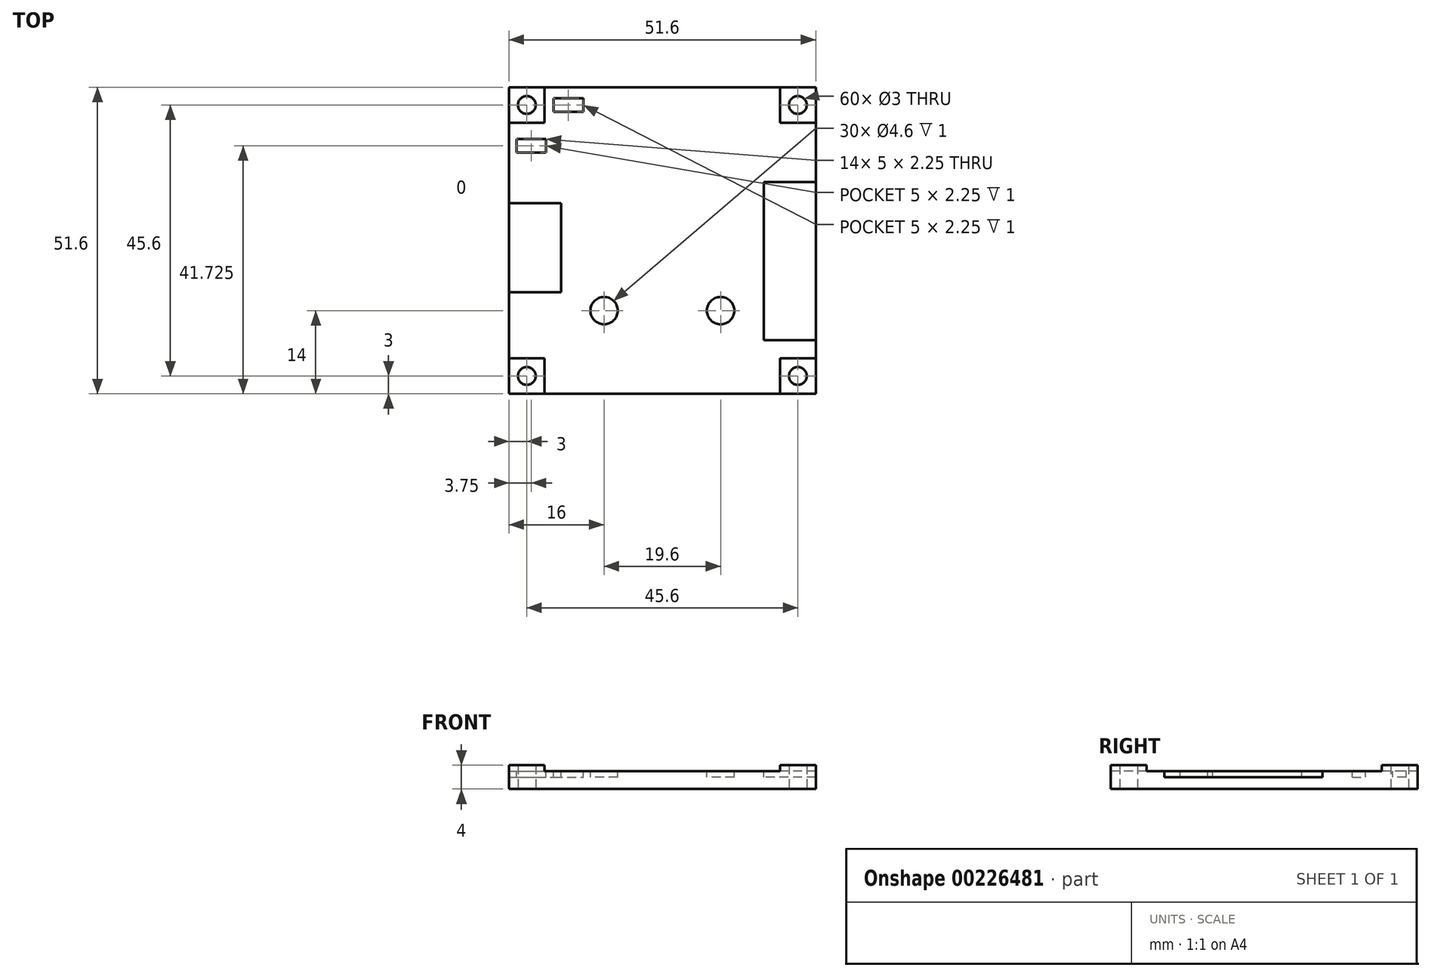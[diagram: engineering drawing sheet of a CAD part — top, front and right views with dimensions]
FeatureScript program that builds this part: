
annotation { "Feature Type Name" : "Feature", "Feature Type Description" : "" }
export const myFeature = defineFeature(function(context is Context, id is Id, definition is map)
    precondition{}
    {
        {
            var Q0;
            Q0=qCreatedBy(makeId("Top.planeOp"),FACE);
            var sketch = newSketch(context, id + "F0", { "sketchPlane" : qUnion([Q0])});
            skLineSegment(sketch, "E0.bottom", {"start": v(0, 0) * mm, "end": v(51.6, 0) * mm});
            skLineSegment(sketch, "E0.top", {"start": v(0, -51.6) * mm, "end": v(51.6, -51.6) * mm});
            skLineSegment(sketch, "E0.left", {"start": v(0, 0) * mm, "end": v(0, -51.6) * mm});
            skLineSegment(sketch, "E0.right", {"start": v(51.6, 0) * mm, "end": v(51.6, -51.6) * mm});
            skCircle(sketch, "E1", {"center": v(3, -3) * mm, "radius": 1.5 * mm});
            skCircle(sketch, "E2", {"center": v(48.6, -3) * mm, "radius": 1.5 * mm});
            skCircle(sketch, "E3", {"center": v(48.6, -48.6) * mm, "radius": 1.5 * mm});
            skCircle(sketch, "E4", {"center": v(3, -48.6) * mm, "radius": 1.5 * mm});
            skLineSegment(sketch, "E5", {"start": v(0, -3) * mm, "end": v(1.5, -3) * mm});
            skLineSegment(sketch, "E6", {"start": v(51.6, -3) * mm, "end": v(50.1, -3) * mm});
            skLineSegment(sketch, "E7", {"start": v(3, -1.5) * mm, "end": v(3, 0) * mm});
            skLineSegment(sketch, "E8", {"start": v(3, -51.6) * mm, "end": v(3, -48.6) * mm});
            skLineSegment(sketch, "E9", {"start": v(3, -48.6) * mm, "end": v(0, -48.6) * mm});
            skLineSegment(sketch, "E10", {"start": v(48.6, -48.6) * mm, "end": v(51.6, -48.6) * mm});
            skLineSegment(sketch, "E11", {"start": v(48.6, -48.6) * mm, "end": v(48.6, -51.6) * mm});
            skLineSegment(sketch, "E12", {"start": v(1.5, -3) * mm, "end": v(3, -3) * mm});
            skLineSegment(sketch, "E13", {"start": v(3, -3) * mm, "end": v(3, -1.5) * mm});
            skLineSegment(sketch, "E14", {"start": v(48.6, -3) * mm, "end": v(50.1, -3) * mm});
            skLineSegment(sketch, "E15", {"start": v(48.6, -3) * mm, "end": v(48.6, 0) * mm});
            skSolve(sketch);
        }
        {
            var Q0;
            {var subQ0=sQuery(id+"F0.wireOp",EDGE,"E5");Q0=makeQuery(id+"F0.imprint","IMPRINT",FACE,{"disambiguationData":[TD([[makeQuery(id+"F0.imprint","IMPRINT",EDGE,{"derivedFrom":subQ0}),-1.0]])]});}
            var Q1;
            {var subQ1=sQuery(id+"F0.wireOp",EDGE,"E0.top");var subQ7=sQuery(id+"F0.wireOp",EDGE,"E0.left");var subQ8=makeQuery(id+"F0.imprint","INTERSECT",VERTEX,{"derivedFrom":[subQ1,subQ7]});Q1=makeQuery(id+"F0.imprint","IMPRINT",FACE,{"disambiguationData":[TD([[makeQuery(id+"F0.imprint","IMPRINT",EDGE,{"disambiguationData":[TD([[subQ8,-1.0]])],"derivedFrom":subQ1}),1.0]])]});}
            var Q2;
            {var subQ1=sQuery(id+"F0.wireOp",EDGE,"E0.right");var subQ7=sQuery(id+"F0.wireOp",EDGE,"E0.top");var subQ8=makeQuery(id+"F0.imprint","INTERSECT",VERTEX,{"derivedFrom":[subQ7,subQ1]});Q2=makeQuery(id+"F0.imprint","IMPRINT",FACE,{"disambiguationData":[TD([[makeQuery(id+"F0.imprint","IMPRINT",EDGE,{"disambiguationData":[TD([[subQ8,1.0]])],"derivedFrom":subQ7}),1.0]])]});}
            var Q3;
            {var subQ0=sQuery(id+"F0.wireOp",EDGE,"E6");Q3=makeQuery(id+"F0.imprint","IMPRINT",FACE,{"disambiguationData":[TD([[makeQuery(id+"F0.imprint","IMPRINT",EDGE,{"derivedFrom":subQ0}),-1.0]])]});}
            var Q4;
            {var subQ0=sQuery(id+"F0.wireOp",EDGE,"E5");Q4=makeQuery(id+"F0.imprint","IMPRINT",FACE,{"disambiguationData":[TD([[makeQuery(id+"F0.imprint","IMPRINT",EDGE,{"derivedFrom":subQ0}),1.0]])]});}
            extrude(context, id + "F1", {"entities" : qUnion([Q0, Q1, Q2, Q3, Q4]), "depth" : 4 * mm});
        }
        {
            var Q0;
            Q0=makeQuery(id+"F1.opExtrude","CAP_FACE",FACE,{"disambiguationData":[OSD([sQuery(id+"F0.wireOp",EDGE,"E0.bottom"),sQuery(id+"F0.wireOp",EDGE,"E0.top"),sQuery(id+"F0.wireOp",EDGE,"E0.left"),sQuery(id+"F0.wireOp",EDGE,"E0.right"),sQuery(id+"F0.wireOp",EDGE,"E1"),sQuery(id+"F0.wireOp",EDGE,"E2"),sQuery(id+"F0.wireOp",EDGE,"E3"),sQuery(id+"F0.wireOp",EDGE,"E4")])],"isStart":false});
            var sketch = newSketch(context, id + "F2", { "sketchPlane" : qUnion([Q0])});
            skLineSegment(sketch, "E16", {"start": v(0, -6) * mm, "end": v(6, -6) * mm});
            skLineSegment(sketch, "E17", {"start": v(6, -6) * mm, "end": v(6, 0) * mm});
            skLineSegment(sketch, "E18", {"start": v(45.6, 0) * mm, "end": v(45.6, -6) * mm});
            skLineSegment(sketch, "E19", {"start": v(45.6, -6) * mm, "end": v(51.6, -6) * mm});
            skLineSegment(sketch, "E20", {"start": v(51.6, -45.6) * mm, "end": v(45.6, -45.6) * mm});
            skLineSegment(sketch, "E21", {"start": v(45.6, -45.6) * mm, "end": v(45.6, -51.6) * mm});
            skLineSegment(sketch, "E22", {"start": v(6, -51.6) * mm, "end": v(6, -45.6) * mm});
            skLineSegment(sketch, "E23", {"start": v(6, -45.6) * mm, "end": v(0, -45.6) * mm});
            skLineSegment(sketch, "E24", {"start": v(51.6, 0) * mm, "end": v(51.6, -16) * mm});
            skLineSegment(sketch, "E25", {"start": v(51.6, -51.6) * mm, "end": v(51.6, -42.6) * mm});
            skLineSegment(sketch, "E26.bottom", {"start": v(51.6, -16) * mm, "end": v(42.85, -16) * mm});
            skLineSegment(sketch, "E26.top", {"start": v(51.6, -42.6) * mm, "end": v(42.85, -42.6) * mm});
            skLineSegment(sketch, "E26.left", {"start": v(51.6, -16) * mm, "end": v(51.6, -42.6) * mm});
            skLineSegment(sketch, "E26.right", {"start": v(42.85, -16) * mm, "end": v(42.85, -42.6) * mm});
            skCircle(sketch, "E27", {"center": v(35.6, -37.6) * mm, "radius": 2.3 * mm});
            skCircle(sketch, "E28", {"center": v(16, -37.6) * mm, "radius": 2.3 * mm});
            skLineSegment(sketch, "E29", {"start": v(16, -37.6) * mm, "end": v(16, -51.6) * mm});
            skLineSegment(sketch, "E30", {"start": v(35.6, -37.6) * mm, "end": v(35.6, -51.6) * mm});
            skLineSegment(sketch, "E31", {"start": v(16, -37.6) * mm, "end": v(0, -37.6) * mm});
            skLineSegment(sketch, "E32", {"start": v(35.6, -37.6) * mm, "end": v(51.6, -37.6) * mm});
            skLineSegment(sketch, "E33.top", {"start": v(7.5, -4.15) * mm, "end": v(12.5, -4.15) * mm});
            skLineSegment(sketch, "E33.left", {"start": v(7.5, -1.9) * mm, "end": v(7.5, -4.15) * mm});
            skLineSegment(sketch, "E33.right", {"start": v(12.5, -1.9) * mm, "end": v(12.5, -4.15) * mm});
            skLineSegment(sketch, "E34", {"start": v(7.5, -1.9) * mm, "end": v(12.5, -1.9) * mm});
            skLineSegment(sketch, "E35.bottom", {"start": v(1.25, -11) * mm, "end": v(6.25, -11) * mm});
            skLineSegment(sketch, "E35.top", {"start": v(1.25, -8.75) * mm, "end": v(6.25, -8.75) * mm});
            skLineSegment(sketch, "E35.left", {"start": v(1.25, -11) * mm, "end": v(1.25, -8.75) * mm});
            skLineSegment(sketch, "E35.right", {"start": v(6.25, -11) * mm, "end": v(6.25, -8.75) * mm});
            skLineSegment(sketch, "E36.bottom", {"start": v(0, -19.5) * mm, "end": v(8.75, -19.5) * mm});
            skLineSegment(sketch, "E36.top", {"start": v(0, -34.5) * mm, "end": v(8.75, -34.5) * mm});
            skLineSegment(sketch, "E36.left", {"start": v(0, -19.5) * mm, "end": v(0, -34.5) * mm});
            skLineSegment(sketch, "E36.right", {"start": v(8.75, -19.5) * mm, "end": v(8.75, -34.5) * mm});
            skSolve(sketch);
        }
        {
            var Q0;
            Q0=makeQuery(id+"F2.imprint","IMPRINT",FACE,{"disambiguationData":[TD([[makeQuery(id+"F2.imprint","IMPRINT",EDGE,{"derivedFrom":sQuery(id+"F2.wireOp",EDGE,"E35.bottom")}),1.0]])]});
            var Q1;
            Q1=makeQuery(id+"F2.imprint","IMPRINT",FACE,{"disambiguationData":[TD([[makeQuery(id+"F2.imprint","IMPRINT",EDGE,{"derivedFrom":sQuery(id+"F2.wireOp",EDGE,"E36.bottom")}),-1.0]])]});
            var Q2;
            {var subQ0=sQuery(id+"F2.wireOp",EDGE,"E29");var subQ1=sQuery(id+"F2.wireOp",EDGE,"E28");var subQ2=makeQuery(id+"F2.imprint","INTERSECT",VERTEX,{"derivedFrom":[subQ1,subQ0]});Q2=makeQuery(id+"F2.imprint","IMPRINT",FACE,{"disambiguationData":[TD([[makeQuery(id+"F2.imprint","IMPRINT",EDGE,{"disambiguationData":[TD([[subQ2,-1.0]])],"derivedFrom":subQ1}),1.0]])]});}
            var Q3;
            {var subQ0=sQuery(id+"F2.wireOp",EDGE,"E29");var subQ1=sQuery(id+"F2.wireOp",EDGE,"E28");var subQ2=makeQuery(id+"F2.imprint","INTERSECT",VERTEX,{"derivedFrom":[subQ1,subQ0]});Q3=makeQuery(id+"F2.imprint","IMPRINT",FACE,{"disambiguationData":[TD([[makeQuery(id+"F2.imprint","IMPRINT",EDGE,{"disambiguationData":[TD([[subQ2,1.0]])],"derivedFrom":subQ1}),1.0]])]});}
            var Q4;
            {var subQ0=sQuery(id+"F2.wireOp",EDGE,"E30");var subQ1=sQuery(id+"F2.wireOp",EDGE,"E27");var subQ2=makeQuery(id+"F2.imprint","INTERSECT",VERTEX,{"derivedFrom":[subQ1,subQ0]});Q4=makeQuery(id+"F2.imprint","IMPRINT",FACE,{"disambiguationData":[TD([[makeQuery(id+"F2.imprint","IMPRINT",EDGE,{"disambiguationData":[TD([[subQ2,-1.0]])],"derivedFrom":subQ1}),1.0]])]});}
            var Q5;
            {var subQ0=sQuery(id+"F2.wireOp",EDGE,"E30");var subQ1=sQuery(id+"F2.wireOp",EDGE,"E27");var subQ2=makeQuery(id+"F2.imprint","INTERSECT",VERTEX,{"derivedFrom":[subQ1,subQ0]});Q5=makeQuery(id+"F2.imprint","IMPRINT",FACE,{"disambiguationData":[TD([[makeQuery(id+"F2.imprint","IMPRINT",EDGE,{"disambiguationData":[TD([[subQ2,1.0]])],"derivedFrom":subQ1}),1.0]])]});}
            var Q6;
            {var subQ0=sQuery(id+"F2.wireOp",EDGE,"E26.bottom");Q6=makeQuery(id+"F2.imprint","IMPRINT",FACE,{"disambiguationData":[TD([[makeQuery(id+"F2.imprint","IMPRINT",EDGE,{"derivedFrom":subQ0}),1.0]])]});}
            var Q7;
            {var subQ0=sQuery(id+"F2.wireOp",EDGE,"E26.top");Q7=makeQuery(id+"F2.imprint","IMPRINT",FACE,{"disambiguationData":[TD([[makeQuery(id+"F2.imprint","IMPRINT",EDGE,{"derivedFrom":subQ0}),-1.0]])]});}
            var Q8;
            Q8=makeQuery(id+"F2.imprint","IMPRINT",FACE,{"disambiguationData":[TD([[makeQuery(id+"F2.imprint","IMPRINT",EDGE,{"derivedFrom":sQuery(id+"F2.wireOp",EDGE,"E33.top")}),1.0]])]});
            extrude(context, id + "F3", {"entities" : qUnion([Q0, Q1, Q2, Q3, Q4, Q5, Q6, Q7, Q8]), "operationType" : NewBodyOperationType.REMOVE, "oppositeDirection" : true, "depth" : 2 * mm});
        }
        {
            var Q0;
            {var subQ7=sQuery(id+"F2.wireOp",EDGE,"E22");Q0=makeQuery(id+"F2.imprint","IMPRINT",FACE,{"disambiguationData":[TD([[makeQuery(id+"F2.imprint","IMPRINT",EDGE,{"derivedFrom":subQ7}),-1.0]])]});}
            var Q1;
            {var subQ24=sQuery(id+"F2.wireOp",EDGE,"E16");Q1=makeQuery(id+"F2.imprint","IMPRINT",FACE,{"disambiguationData":[TD([[makeQuery(id+"F2.imprint","IMPRINT",EDGE,{"derivedFrom":subQ24}),-1.0]])]});}
            var Q2;
            {var subQ2=sQuery(id+"F2.wireOp",EDGE,"E20");Q2=makeQuery(id+"F2.imprint","IMPRINT",FACE,{"disambiguationData":[TD([[makeQuery(id+"F2.imprint","IMPRINT",EDGE,{"derivedFrom":subQ2}),-1.0]])]});}
            extrude(context, id + "F4", {"entities" : qUnion([Q0, Q1, Q2]), "operationType" : NewBodyOperationType.REMOVE, "oppositeDirection" : true, "depth" : 1 * mm});
        }
    });
